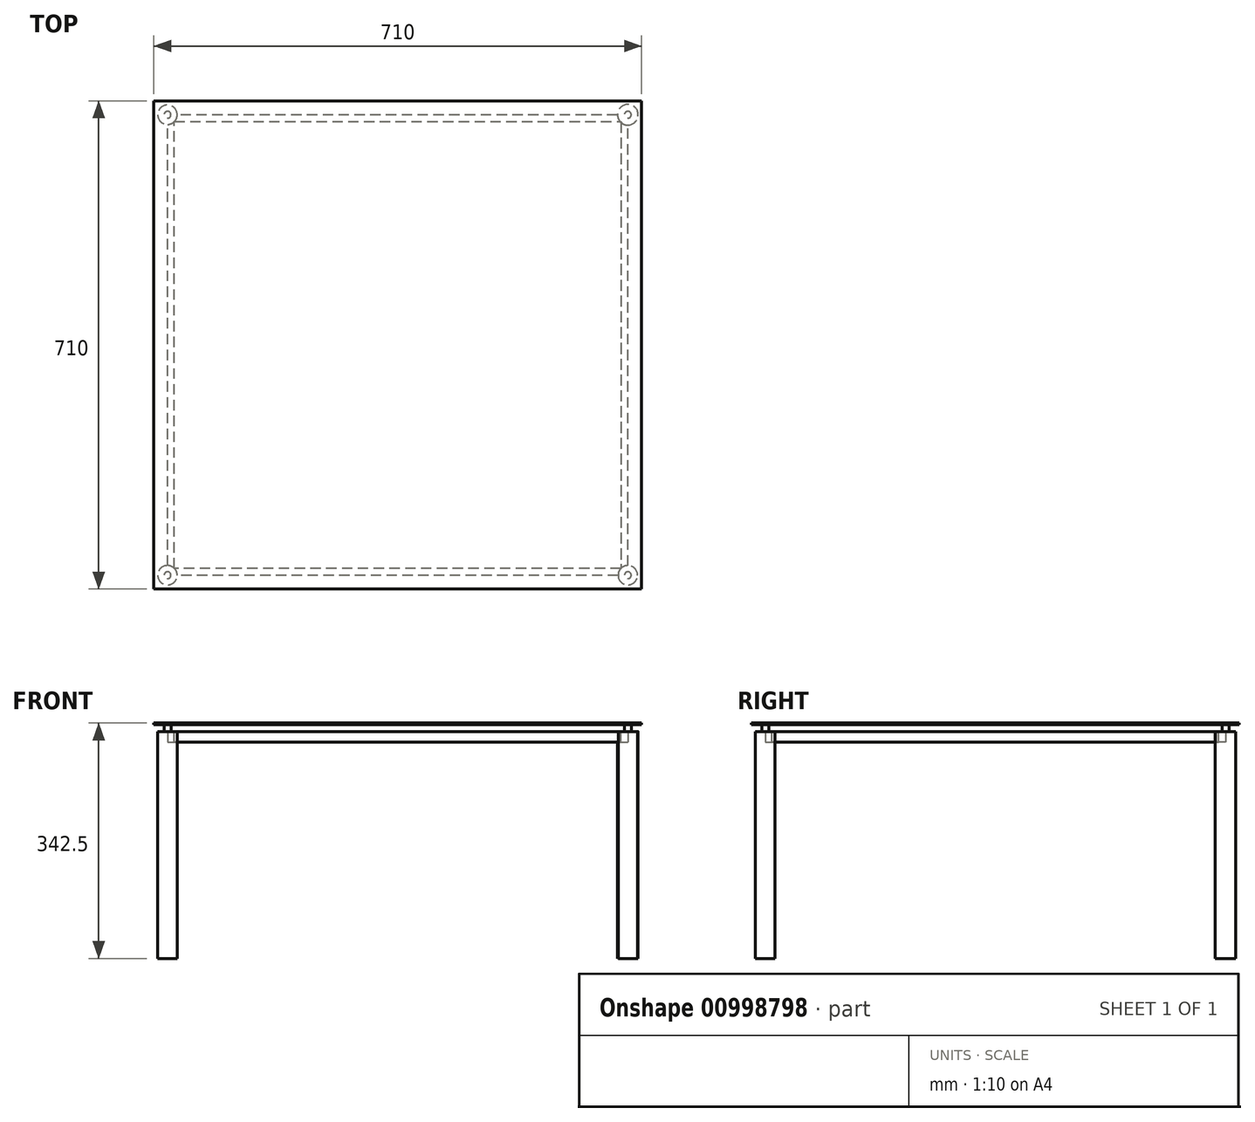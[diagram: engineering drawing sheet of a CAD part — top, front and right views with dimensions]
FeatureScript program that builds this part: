
annotation { "Feature Type Name" : "Feature", "Feature Type Description" : "" }
export const myFeature = defineFeature(function(context is Context, id is Id, definition is map)
    precondition{}
    {
        {
            var Q0;
            Q0=qCreatedBy(makeId("Top.planeOp"),FACE);
            var sketch = newSketch(context, id + "F0", { "sketchPlane" : qUnion([Q0])});
            skLineSegment(sketch, "E0.bottom", {"start": v(335, -335) * mm, "end": v(-335, -335) * mm});
            skLineSegment(sketch, "E0.top", {"start": v(335, 335) * mm, "end": v(-335, 335) * mm});
            skLineSegment(sketch, "E0.left", {"start": v(335, -335) * mm, "end": v(335, 335) * mm});
            skLineSegment(sketch, "E0.right", {"start": v(-335, -335) * mm, "end": v(-335, 335) * mm});
            skPoint(sketch, "E0.middle", {"position": v(0, 0) * mm});
            skSolve(sketch);
        }
        {
            var Q0;
            Q0=makeQuery(id+"F0.imprint","IMPRINT",FACE,{"disambiguationData":[TD([[makeQuery(id+"F0.imprint","IMPRINT",EDGE,{"derivedFrom":sQuery(id+"F0.wireOp",EDGE,"E0.bottom")}),-1.0]])]});
            extrude(context, id + "F1", {"entities" : qUnion([Q0]), "depth" : 15 * mm, "offsetDistance" : 25 * mm});
        }
        {
            var Q0;
            Q0=makeQuery(id+"F1.opExtrude","CAP_FACE",FACE,{"disambiguationData":[OSD([sQuery(id+"F0.wireOp",EDGE,"E0.bottom"),sQuery(id+"F0.wireOp",EDGE,"E0.top"),sQuery(id+"F0.wireOp",EDGE,"E0.left"),sQuery(id+"F0.wireOp",EDGE,"E0.right")])],"isStart":false});
            var sketch = newSketch(context, id + "F2", { "sketchPlane" : qUnion([Q0])});
            skLineSegment(sketch, "E1", {"start": v(325, -325) * mm, "end": v(-325, -325) * mm});
            skLineSegment(sketch, "E2", {"start": v(-325, -325) * mm, "end": v(-325, 325) * mm});
            skLineSegment(sketch, "E3", {"start": v(-325, 325) * mm, "end": v(325, 325) * mm});
            skLineSegment(sketch, "E4", {"start": v(325, 325) * mm, "end": v(325, -325) * mm});
            skSolve(sketch);
        }
        {
            var Q0;
            Q0=makeQuery(id+"F2.imprint","IMPRINT",FACE,{"disambiguationData":[TD([[makeQuery(id+"F2.imprint","IMPRINT",EDGE,{"derivedFrom":sQuery(id+"F2.wireOp",EDGE,"E1")}),-1.0]])]});
            extrude(context, id + "F3", {"entities" : qUnion([Q0]), "operationType" : NewBodyOperationType.REMOVE, "endBound" : BoundingType.THROUGH_ALL, "oppositeDirection" : true, "depth" : 25 * mm, "offsetDistance" : 25 * mm});
        }
        {
            var Q0;
            Q0=makeQuery(id+"F1.opExtrude","CAP_FACE",FACE,{"disambiguationData":[OSD([sQuery(id+"F0.wireOp",EDGE,"E0.bottom"),sQuery(id+"F0.wireOp",EDGE,"E0.top"),sQuery(id+"F0.wireOp",EDGE,"E0.left"),sQuery(id+"F0.wireOp",EDGE,"E0.right")])],"isStart":true});
            var sketch = newSketch(context, id + "F4", { "sketchPlane" : qUnion([Q0])});
            skCircle(sketch, "E5", {"center": v(335, -335) * mm, "radius": 15 * mm});
            skSolve(sketch);
        }
        {
            var Q0;
            {var subQ0=sQuery(id+"F0.wireOp",EDGE,"E0.left");var subQ1=makeQuery(id+"F1.opExtrude","CAP_EDGE",EDGE,{"disambiguationData":[OSD([subQ0])],"isStart":true});var subQ2=sQuery(id+"F0.wireOp",EDGE,"E0.top");var subQ3=makeQuery(id+"F1.opExtrude","CAP_EDGE",EDGE,{"disambiguationData":[OSD([subQ2])],"isStart":true});var subQ4=makeQuery(id+"F4.imprint","INTERSECT",VERTEX,{"derivedFrom":[subQ3,subQ1]});Q0=makeQuery(id+"F4.imprint","IMPRINT",FACE,{"disambiguationData":[TD([[makeQuery(id+"F4.imprint","IMPRINT",EDGE,{"disambiguationData":[TD([[subQ4,-1.0]])],"derivedFrom":subQ3}),-1.0]])]});}
            var Q1;
            {var subQ0=sQuery(id+"F4.wireOp",EDGE,"E5");var subQ1=makeQuery(id+"F1.opExtrude","CAP_FACE",FACE,{"disambiguationData":[OSD([sQuery(id+"F0.wireOp",EDGE,"E0.bottom"),sQuery(id+"F0.wireOp",EDGE,"E0.top"),sQuery(id+"F0.wireOp",EDGE,"E0.left"),sQuery(id+"F0.wireOp",EDGE,"E0.right")])],"isStart":true});var subQ2=makeQuery(id+"F3.boolean.opBoolean","INTERSECT",EDGE,{"derivedFrom":[subQ1,makeQuery(id+"F3.opExtrude","SWEPT_FACE",FACE,{"disambiguationData":[OSD([sQuery(id+"F2.wireOp",EDGE,"E4")])]})]});var subQ3=makeQuery(id+"F4.imprint","INTERSECT",VERTEX,{"derivedFrom":[subQ2,subQ0]});Q1=makeQuery(id+"F4.imprint","IMPRINT",FACE,{"disambiguationData":[TD([[makeQuery(id+"F4.imprint","IMPRINT",EDGE,{"disambiguationData":[TD([[subQ3,-1.0]])],"derivedFrom":subQ0}),1.0]])]});}
            var Q2;
            {var subQ0=sQuery(id+"F4.wireOp",EDGE,"E5");var subQ1=makeQuery(id+"F1.opExtrude","CAP_EDGE",EDGE,{"disambiguationData":[OSD([sQuery(id+"F0.wireOp",EDGE,"E0.left")])],"isStart":true});var subQ2=makeQuery(id+"F4.imprint","INTERSECT",VERTEX,{"derivedFrom":[subQ1,subQ0]});Q2=makeQuery(id+"F4.imprint","IMPRINT",FACE,{"disambiguationData":[TD([[makeQuery(id+"F4.imprint","IMPRINT",EDGE,{"disambiguationData":[TD([[subQ2,1.0]])],"derivedFrom":subQ0}),1.0]])]});}
            extrude(context, id + "F5", {"entities" : qUnion([Q0, Q1, Q2]), "operationType" : NewBodyOperationType.ADD, "depth" : 315 * mm, "offsetDistance" : 25 * mm});
        }
        {
            var Q0;
            {var subQ1=sQuery(id+"F0.wireOp",EDGE,"E0.top");var subQ2=sQuery(id+"F4.wireOp",EDGE,"E5");Q0=makeQuery(id+"F5.boolean.opBoolean","SPLIT",FACE,{"disambiguationData":[TD([makeQuery(id+"F1.opExtrude","SWEPT_FACE",FACE,{"disambiguationData":[OSD([subQ1])]})])],"derivedFrom":makeQuery(id+"F5.opExtrude","CAP_FACE",FACE,{"disambiguationData":[OSD([subQ2])],"isStart":true})});}
            extrude(context, id + "F6", {"entities" : qUnion([Q0]), "operationType" : NewBodyOperationType.ADD, "depth" : 15 * mm, "offsetDistance" : 25 * mm});
        }
        {
            var Q0;
            Q0=makeQuery(id+"F6.boolean.opBoolean","MERGE",FACE,{"derivedFrom":[makeQuery(id+"F1.opExtrude","CAP_FACE",FACE,{"disambiguationData":[OSD([sQuery(id+"F0.wireOp",EDGE,"E0.bottom"),sQuery(id+"F0.wireOp",EDGE,"E0.top"),sQuery(id+"F0.wireOp",EDGE,"E0.left"),sQuery(id+"F0.wireOp",EDGE,"E0.right")])],"isStart":false}),makeQuery(id+"F6.opExtrude","CAP_FACE",FACE,{"disambiguationData":[OSD([sQuery(id+"F4.wireOp",EDGE,"E5")])],"isStart":false})]});
            var sketch = newSketch(context, id + "F7", { "sketchPlane" : qUnion([Q0])});
            skCircle(sketch, "E6", {"center": v(335, 335) * mm, "radius": 5 * mm});
            skSolve(sketch);
        }
        {
            var Q0;
            Q0=makeQuery(id+"F7.imprint","IMPRINT",FACE,{"disambiguationData":[TD([[makeQuery(id+"F7.imprint","IMPRINT",EDGE,{"derivedFrom":sQuery(id+"F7.wireOp",EDGE,"E6")}),1.0]])]});
            extrude(context, id + "F8", {"entities" : qUnion([Q0]), "operationType" : NewBodyOperationType.ADD, "depth" : 10 * mm, "offsetDistance" : 25 * mm});
        }
        {
            var Q0;
            Q0=makeQuery(id+"F1.opExtrude","CAP_FACE",FACE,{"disambiguationData":[OSD([sQuery(id+"F0.wireOp",EDGE,"E0.bottom"),sQuery(id+"F0.wireOp",EDGE,"E0.top"),sQuery(id+"F0.wireOp",EDGE,"E0.left"),sQuery(id+"F0.wireOp",EDGE,"E0.right")])],"isStart":true});
            var sketch = newSketch(context, id + "F9", { "sketchPlane" : qUnion([Q0])});
            skCircle(sketch, "E7", {"center": v(-335, -335) * mm, "radius": 14.14 * mm});
            skSolve(sketch);
        }
        {
            var Q0;
            {var subQ0=sQuery(id+"F9.wireOp",EDGE,"E7");var subQ1=sQuery(id+"F0.wireOp",EDGE,"E0.right");var subQ5=makeQuery(id+"F1.opExtrude","CAP_EDGE",EDGE,{"disambiguationData":[OSD([subQ1])],"isStart":true});var subQ6=makeQuery(id+"F9.imprint","INTERSECT",VERTEX,{"derivedFrom":[subQ5,subQ0]});Q0=makeQuery(id+"F9.imprint","IMPRINT",FACE,{"disambiguationData":[TD([[makeQuery(id+"F9.imprint","IMPRINT",EDGE,{"disambiguationData":[TD([[subQ6,-1.0]])],"derivedFrom":subQ0}),1.0]])]});}
            var Q1;
            {var subQ0=sQuery(id+"F9.wireOp",EDGE,"E7");var subQ1=sQuery(id+"F0.wireOp",EDGE,"E0.right");var subQ8=makeQuery(id+"F1.opExtrude","CAP_EDGE",EDGE,{"disambiguationData":[OSD([subQ1])],"isStart":true});var subQ9=makeQuery(id+"F9.imprint","INTERSECT",VERTEX,{"derivedFrom":[subQ8,subQ0]});Q1=makeQuery(id+"F9.imprint","IMPRINT",FACE,{"disambiguationData":[TD([[makeQuery(id+"F9.imprint","IMPRINT",EDGE,{"disambiguationData":[TD([[subQ9,-1.0]])],"derivedFrom":subQ8}),1.0]])]});}
            extrude(context, id + "F10", {"entities" : qUnion([Q0, Q1]), "operationType" : NewBodyOperationType.ADD, "depth" : 315 * mm, "offsetDistance" : 25 * mm});
        }
        {
            var Q0;
            Q0=makeQuery(id+"F10.opExtrude","CAP_FACE",FACE,{"disambiguationData":[OSD([sQuery(id+"F9.wireOp",EDGE,"E7")])],"isStart":true});
            extrude(context, id + "F11", {"entities" : qUnion([Q0]), "operationType" : NewBodyOperationType.ADD, "depth" : 15 * mm, "offsetDistance" : 25 * mm});
        }
        {
            var Q0;
            Q0=makeQuery(id+"F11.boolean.opBoolean","MERGE",FACE,{"derivedFrom":[makeQuery(id+"F6.boolean.opBoolean","MERGE",FACE,{"derivedFrom":[makeQuery(id+"F1.opExtrude","CAP_FACE",FACE,{"disambiguationData":[OSD([sQuery(id+"F0.wireOp",EDGE,"E0.bottom"),sQuery(id+"F0.wireOp",EDGE,"E0.top"),sQuery(id+"F0.wireOp",EDGE,"E0.left"),sQuery(id+"F0.wireOp",EDGE,"E0.right")])],"isStart":false}),makeQuery(id+"F6.opExtrude","CAP_FACE",FACE,{"disambiguationData":[OSD([sQuery(id+"F4.wireOp",EDGE,"E5")])],"isStart":false})]}),makeQuery(id+"F11.opExtrude","CAP_FACE",FACE,{"disambiguationData":[OSD([sQuery(id+"F9.wireOp",EDGE,"E7")])],"isStart":false})]});
            var sketch = newSketch(context, id + "F12", { "sketchPlane" : qUnion([Q0])});
            skCircle(sketch, "E8", {"center": v(-335, 335) * mm, "radius": 5 * mm});
            skSolve(sketch);
        }
        {
            var Q0;
            Q0=makeQuery(id+"F12.imprint","IMPRINT",FACE,{"disambiguationData":[TD([[makeQuery(id+"F12.imprint","IMPRINT",EDGE,{"derivedFrom":sQuery(id+"F12.wireOp",EDGE,"E8")}),1.0]])]});
            var Q1;
            Q1=sQuery(id+"F12.wireOp",EDGE,"E8");
            extrude(context, id + "F13", {"entities" : qUnion([Q0]), "operationType" : NewBodyOperationType.ADD, "surfaceEntities" : qUnion([Q1]), "depth" : 10 * mm, "offsetDistance" : 25 * mm});
        }
        {
            var Q0;
            {var subQ1=sQuery(id+"F0.wireOp",EDGE,"E0.bottom");var subQ2=sQuery(id+"F0.wireOp",EDGE,"E0.right");var subQ3=sQuery(id+"F0.wireOp",EDGE,"E0.left");var subQ4=makeQuery(id+"F1.opExtrude","CAP_FACE",FACE,{"disambiguationData":[OSD([subQ1,sQuery(id+"F0.wireOp",EDGE,"E0.top"),subQ3,subQ2])],"isStart":true});Q0=makeQuery(id+"F10.boolean.opBoolean","SPLIT",FACE,{"disambiguationData":[TD([makeQuery(id+"F1.opExtrude","SWEPT_FACE",FACE,{"disambiguationData":[OSD([subQ1])]})])],"derivedFrom":subQ4});}
            var sketch = newSketch(context, id + "F14", { "sketchPlane" : qUnion([Q0])});
            skCircle(sketch, "E9", {"center": v(-335, 335) * mm, "radius": 14.14 * mm});
            skSolve(sketch);
        }
        {
            var Q0;
            {var subQ0=sQuery(id+"F14.wireOp",EDGE,"E9");var subQ2=sQuery(id+"F0.wireOp",EDGE,"E0.bottom");var subQ5=makeQuery(id+"F1.opExtrude","CAP_EDGE",EDGE,{"disambiguationData":[OSD([subQ2])],"isStart":true});var subQ6=makeQuery(id+"F14.imprint","INTERSECT",VERTEX,{"derivedFrom":[subQ5,subQ0]});Q0=makeQuery(id+"F14.imprint","IMPRINT",FACE,{"disambiguationData":[TD([[makeQuery(id+"F14.imprint","IMPRINT",EDGE,{"disambiguationData":[TD([[subQ6,-1.0]])],"derivedFrom":subQ0}),1.0]])]});}
            var Q1;
            {var subQ0=sQuery(id+"F14.wireOp",EDGE,"E9");var subQ2=sQuery(id+"F0.wireOp",EDGE,"E0.bottom");var subQ7=makeQuery(id+"F1.opExtrude","CAP_EDGE",EDGE,{"disambiguationData":[OSD([subQ2])],"isStart":true});var subQ8=makeQuery(id+"F14.imprint","INTERSECT",VERTEX,{"derivedFrom":[subQ7,subQ0]});Q1=makeQuery(id+"F14.imprint","IMPRINT",FACE,{"disambiguationData":[TD([[makeQuery(id+"F14.imprint","IMPRINT",EDGE,{"disambiguationData":[TD([[subQ8,-1.0]])],"derivedFrom":subQ7}),1.0]])]});}
            extrude(context, id + "F15", {"entities" : qUnion([Q0, Q1]), "operationType" : NewBodyOperationType.ADD, "depth" : 315 * mm, "offsetDistance" : 25 * mm});
        }
        {
            var Q0;
            Q0=makeQuery(id+"F15.opExtrude","CAP_FACE",FACE,{"disambiguationData":[OSD([sQuery(id+"F14.wireOp",EDGE,"E9")])],"isStart":true});
            extrude(context, id + "F16", {"entities" : qUnion([Q0]), "operationType" : NewBodyOperationType.ADD, "depth" : 15 * mm, "offsetDistance" : 25 * mm});
        }
        {
            var Q0;
            Q0=makeQuery(id+"F16.boolean.opBoolean","MERGE",FACE,{"derivedFrom":[makeQuery(id+"F11.boolean.opBoolean","MERGE",FACE,{"derivedFrom":[makeQuery(id+"F6.boolean.opBoolean","MERGE",FACE,{"derivedFrom":[makeQuery(id+"F1.opExtrude","CAP_FACE",FACE,{"disambiguationData":[OSD([sQuery(id+"F0.wireOp",EDGE,"E0.bottom"),sQuery(id+"F0.wireOp",EDGE,"E0.top"),sQuery(id+"F0.wireOp",EDGE,"E0.left"),sQuery(id+"F0.wireOp",EDGE,"E0.right")])],"isStart":false}),makeQuery(id+"F6.opExtrude","CAP_FACE",FACE,{"disambiguationData":[OSD([sQuery(id+"F4.wireOp",EDGE,"E5")])],"isStart":false})]}),makeQuery(id+"F11.opExtrude","CAP_FACE",FACE,{"disambiguationData":[OSD([sQuery(id+"F9.wireOp",EDGE,"E7")])],"isStart":false})]}),makeQuery(id+"F16.opExtrude","CAP_FACE",FACE,{"disambiguationData":[OSD([sQuery(id+"F14.wireOp",EDGE,"E9")])],"isStart":false})]});
            var sketch = newSketch(context, id + "F17", { "sketchPlane" : qUnion([Q0])});
            skCircle(sketch, "E10", {"center": v(-335, -335) * mm, "radius": 5 * mm});
            skSolve(sketch);
        }
        {
            var Q0;
            Q0=makeQuery(id+"F17.imprint","IMPRINT",FACE,{"disambiguationData":[TD([[makeQuery(id+"F17.imprint","IMPRINT",EDGE,{"derivedFrom":sQuery(id+"F17.wireOp",EDGE,"E10")}),1.0]])]});
            extrude(context, id + "F18", {"entities" : qUnion([Q0]), "operationType" : NewBodyOperationType.ADD, "depth" : 10 * mm, "offsetDistance" : 25 * mm});
        }
        {
            var Q0;
            {var subQ7=sQuery(id+"F0.wireOp",EDGE,"E0.bottom");var subQ8=makeQuery(id+"F1.opExtrude","SWEPT_FACE",FACE,{"disambiguationData":[OSD([subQ7])]});var subQ9=sQuery(id+"F0.wireOp",EDGE,"E0.right");var subQ10=sQuery(id+"F0.wireOp",EDGE,"E0.left");var subQ11=makeQuery(id+"F1.opExtrude","CAP_FACE",FACE,{"disambiguationData":[OSD([subQ7,sQuery(id+"F0.wireOp",EDGE,"E0.top"),subQ10,subQ9])],"isStart":true});Q0=makeQuery(id+"F15.boolean.opBoolean","SPLIT",FACE,{"disambiguationData":[TD([subQ8])],"derivedFrom":makeQuery(id+"F10.boolean.opBoolean","SPLIT",FACE,{"disambiguationData":[TD([subQ8])],"derivedFrom":subQ11})});}
            var sketch = newSketch(context, id + "F19", { "sketchPlane" : qUnion([Q0])});
            skCircle(sketch, "E11", {"center": v(335, 335) * mm, "radius": 14.14 * mm});
            skSolve(sketch);
        }
        {
            var Q0;
            Q0=makeQuery(id+"FVAg2lP2gIzFbRm_1.boolean.opBoolean","MERGE",FACE,{"derivedFrom":[makeQuery(id+"F16.boolean.opBoolean","MERGE",FACE,{"derivedFrom":[makeQuery(id+"F11.boolean.opBoolean","MERGE",FACE,{"derivedFrom":[makeQuery(id+"F6.boolean.opBoolean","MERGE",FACE,{"derivedFrom":[makeQuery(id+"F1.opExtrude","CAP_FACE",FACE,{"disambiguationData":[OSD([sQuery(id+"F0.wireOp",EDGE,"E0.bottom"),sQuery(id+"F0.wireOp",EDGE,"E0.top"),sQuery(id+"F0.wireOp",EDGE,"E0.left"),sQuery(id+"F0.wireOp",EDGE,"E0.right")])],"isStart":false}),makeQuery(id+"F6.opExtrude","CAP_FACE",FACE,{"disambiguationData":[OSD([sQuery(id+"F4.wireOp",EDGE,"E5")])],"isStart":false})]}),makeQuery(id+"F11.opExtrude","CAP_FACE",FACE,{"disambiguationData":[OSD([sQuery(id+"F9.wireOp",EDGE,"E7")])],"isStart":false})]}),makeQuery(id+"F16.opExtrude","CAP_FACE",FACE,{"disambiguationData":[OSD([sQuery(id+"F14.wireOp",EDGE,"E9")])],"isStart":false})]}),makeQuery(id+"FVAg2lP2gIzFbRm_1.opExtrude","CAP_FACE",FACE,{"disambiguationData":[OSD([sQuery(id+"F19.wireOp",EDGE,"E11")])],"isStart":false})]});
            var sketch = newSketch(context, id + "F20", { "sketchPlane" : qUnion([Q0])});
            skCircle(sketch, "E12", {"center": v(335, -335) * mm, "radius": 5 * mm});
            skSolve(sketch);
        }
        {
            var Q0;
            Q0=makeQuery(id+"F20.imprint","IMPRINT",FACE,{"disambiguationData":[TD([[makeQuery(id+"F20.imprint","IMPRINT",EDGE,{"derivedFrom":sQuery(id+"F20.wireOp",EDGE,"E12")}),1.0]])]});
            extrude(context, id + "F21", {"entities" : qUnion([Q0]), "operationType" : NewBodyOperationType.ADD, "depth" : 10 * mm, "offsetDistance" : 25 * mm});
        }
        {
            var Q0;
            {var subQ0=sQuery(id+"F19.wireOp",EDGE,"E11");var subQ1=sQuery(id+"F0.wireOp",EDGE,"E0.bottom");var subQ2=sQuery(id+"F0.wireOp",EDGE,"E0.left");var subQ3=makeQuery(id+"F1.opExtrude","CAP_FACE",FACE,{"disambiguationData":[OSD([subQ1,sQuery(id+"F0.wireOp",EDGE,"E0.top"),subQ2,sQuery(id+"F0.wireOp",EDGE,"E0.right")])],"isStart":true});var subQ4=makeQuery(id+"F15.boolean.opBoolean","SPLIT",EDGE,{"disambiguationData":[topologyDisambiguationEdgeConnected([subQ3])],"derivedFrom":makeQuery(id+"F1.opExtrude","CAP_EDGE",EDGE,{"disambiguationData":[OSD([subQ1])],"isStart":true})});var subQ5=makeQuery(id+"F19.imprint","INTERSECT",VERTEX,{"derivedFrom":[subQ4,subQ0]});Q0=makeQuery(id+"F19.imprint","IMPRINT",FACE,{"disambiguationData":[TD([[makeQuery(id+"F19.imprint","IMPRINT",EDGE,{"disambiguationData":[TD([[subQ5,1.0]])],"derivedFrom":subQ0}),1.0]])]});}
            var Q1;
            {var subQ0=sQuery(id+"F19.wireOp",EDGE,"E11");var subQ1=sQuery(id+"F0.wireOp",EDGE,"E0.left");var subQ2=sQuery(id+"F0.wireOp",EDGE,"E0.bottom");var subQ3=makeQuery(id+"F1.opExtrude","CAP_FACE",FACE,{"disambiguationData":[OSD([subQ2,sQuery(id+"F0.wireOp",EDGE,"E0.top"),subQ1,sQuery(id+"F0.wireOp",EDGE,"E0.right")])],"isStart":true});var subQ6=makeQuery(id+"F15.boolean.opBoolean","SPLIT",EDGE,{"disambiguationData":[topologyDisambiguationEdgeConnected([subQ3])],"derivedFrom":makeQuery(id+"F1.opExtrude","CAP_EDGE",EDGE,{"disambiguationData":[OSD([subQ2])],"isStart":true})});var subQ7=makeQuery(id+"F19.imprint","INTERSECT",VERTEX,{"derivedFrom":[subQ6,subQ0]});Q1=makeQuery(id+"F19.imprint","IMPRINT",FACE,{"disambiguationData":[TD([[makeQuery(id+"F19.imprint","IMPRINT",EDGE,{"disambiguationData":[TD([[subQ7,-1.0]])],"derivedFrom":subQ0}),1.0]])]});}
            extrude(context, id + "F22", {"entities" : qUnion([Q0, Q1]), "operationType" : NewBodyOperationType.ADD, "depth" : 315 * mm, "offsetDistance" : 25 * mm});
        }
        {
            var Q0;
            Q0=makeQuery(id+"F22.opExtrude","CAP_FACE",FACE,{"disambiguationData":[OSD([sQuery(id+"F19.wireOp",EDGE,"E11")])],"isStart":true});
            extrude(context, id + "F23", {"entities" : qUnion([Q0]), "operationType" : NewBodyOperationType.ADD, "depth" : 15 * mm, "offsetDistance" : 25 * mm});
        }
        {
            var Q0;
            Q0=makeQuery(id+"F13.opExtrude","CAP_FACE",FACE,{"disambiguationData":[OSD([sQuery(id+"F12.wireOp",EDGE,"E8")])],"isStart":false});
            var sketch = newSketch(context, id + "F24", { "sketchPlane" : qUnion([Q0])});
            skLineSegment(sketch, "E13", {"start": v(-355, 355) * mm, "end": v(355, 355) * mm});
            skLineSegment(sketch, "E14", {"start": v(355, 355) * mm, "end": v(355, -355) * mm});
            skLineSegment(sketch, "E15", {"start": v(355, -355) * mm, "end": v(-355, -355) * mm});
            skLineSegment(sketch, "E16", {"start": v(-355, -355) * mm, "end": v(-355, 355) * mm});
            skSolve(sketch);
        }
        {
            var Q0;
            Q0=makeQuery(id+"F24.imprint","IMPRINT",FACE,{"disambiguationData":[TD([[makeQuery(id+"F24.imprint","IMPRINT",EDGE,{"derivedFrom":sQuery(id+"F24.wireOp",EDGE,"E13")}),-1.0]])]});
            var Q1;
            Q1=makeQuery(id+"F24.imprint","IMPRINT",FACE,{"disambiguationData":[TD([[makeQuery(id+"F24.imprint","IMPRINT",EDGE,{"derivedFrom":makeQuery(id+"F13.opExtrude","CAP_EDGE",EDGE,{"disambiguationData":[OSD([sQuery(id+"F12.wireOp",EDGE,"E8")])],"isStart":false})}),1.0]])]});
            extrude(context, id + "F25", {"entities" : qUnion([Q0, Q1]), "operationType" : NewBodyOperationType.ADD, "depth" : 2.5 * mm, "offsetDistance" : 25 * mm});
        }
    });
